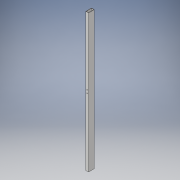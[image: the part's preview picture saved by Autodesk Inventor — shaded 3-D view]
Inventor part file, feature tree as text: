
AUTODESK INVENTOR PART (.ipt)
format: ipt  version: 2017 (Build 210142000, 142)  size: 115,200 bytes
history: native  units: in
note: dims shown in document units (in); Inventor stores cm internally (conversion verified against a paired STEP export)
features: extrude x2, sketch x2
ambient origin geometry x8: Origin, YZ Plane, XZ Plane, XY Plane, X Axis, Y Axis, Z Axis, Center Point
bodies: Solid1 (feature_tree)
feature tree (4):
  extrude  "Extrusion1"  Depth=2.0in
  extrude  "Extrusion2"  Depth=1.75in
  sketch  "Sketch2"  dims[d2=1.0in d3=2.0in]
  sketch  "Sketch3"  dims[d4=0.75in d5=1.75in d6=0.125in d7=0.125in d8=48.0in d9=0.0in d10=48.0in d11=24.0in d12=0.5in d13=0.25in d14=48.0in d15=0.0in]
